# Revit family: 81MAJB-81MBJB-81MCJB-81MDJB_MC Chair_Upholstered Seat Pad Back No Armrest Silver Frame Black Shell_1
name_source: partatom
category: Furniture
revit_build: Autodesk Revit 2017 (Build: 20160225_1515(x64)
units: mm (PartAtom-declared; Revit-internal decimal feet)

## family parameters
Always vertical = Yes
Cut with Voids When Loaded = No
OmniClass Number = 23.40.20.00
OmniClass Title = General Furniture and Specialties
Room Calculation Point = No
Shared = No
Work Plane-Based = No

## types (48) — shared parameters
Assembly Code = E2020200
Caster = okm_G155
D = 580 mm  [stored 1.90289 ft]
Frame = okm_silver FX4
H = 850 mm  [stored 2.78871 ft]
Keynote = 12490
Kind = Chair
Manufacturer = Okamura Corporation
Product Categories = Multi-Purpose Chair
Shell = okm_G721
URL = http://www.okamura.co.jp
W = 596 mm  [stored 1.95538 ft]

## per-type parameters (varying)
| type | Back & Seat | Product Number |
| FEA3（White）_Without Brake Hard Caster | okm_FEA3 | 81MAJB |
| FEA2(Beige)_Without Brake Hard Caster | okm_FEA2 | 81MAJB |
| FGE8(Dark Brown)_Without Brake Hard Caster | okm_FGE8 | 81MAJB |
| FBA3(Light Gray)_Without Brake Hard Caster | okm_FBA3 | 81MAJB |
| FPE2(Medium Gray)_Without Brake Hard Caster | okm_FPE2 | 81MAJB |
| FBA1(Black)_Without Brake Hard Caster | okm_FBA1 | 81MAJB |
| FEA0(Purple)_Without Brake Hard Caster | okm_FEA0 | 81MAJB |
| FBA4(Dark Blue)_Without Brake Hard Caster | okm_FBA4 | 81MAJB |
| FPE6(Sage)_Without Brake Hard Caster | okm_FPE6 | 81MAJB |
| FPE5(Dark Green)_Without Brake Hard Caster | okm_FPE5 | 81MAJB |
| FPE8(Orange Red)_Without Brake Hard Caster | okm_FPE8 | 81MAJB |
| FPE9(Red)_Without Brake Hard Caster | okm_FPE9 | 81MAJB |
| FEA3（White）_With Brake Hard Caster | okm_FEA3 | 81MBJB |
| FEA2(Beige)_With Brake Hard Caster | okm_FEA2 | 81MBJB |
| FGE8(Dark Brown)_With Brake Hard Caster | okm_FGE8 | 81MBJB |
| FBA3(Light Gray)_With Brake Hard Caster | okm_FBA3 | 81MBJB |
| FPE2(Medium Gray)_With Brake Hard Caster | okm_FPE2 | 81MBJB |
| FBA1(Black)_With Brake Hard Caster | okm_FBA1 | 81MBJB |
| FEA0(Purple)_With Brake Hard Caster | okm_FEA0 | 81MBJB |
| FBA4(Dark Blue)_With Brake Hard Caster | okm_FBA4 | 81MBJB |
| FPE6(Sage)_With Brake Hard Caster | okm_FPE6 | 81MBJB |
| FPE5(Dark Green)_With Brake Hard Caster | okm_FPE5 | 81MBJB |
| FPE8(Orange Red)_With Brake Hard Caster | okm_FPE8 | 81MBJB |
| FPE9(Red)_With Brake Hard Caster | okm_FPE9 | 81MBJB |
| FEA3（White）_Without Brake Soft Caster | okm_FEA3 | 81MCJB |
| FEA2(Beige)_Without Brake Soft Caster | okm_FEA2 | 81MCJB |
| FGE8(Dark Brown)_Without Brake Soft Caster | okm_FGE8 | 81MCJB |
| FBA3(Light Gray)_Without Brake Soft Caster | okm_FBA3 | 81MCJB |
| FPE2(Medium Gray)_Without Brake Soft Caster | okm_FPE2 | 81MCJB |
| FBA1(Black)_Without Brake Soft Caster | okm_FBA1 | 81MCJB |
| FEA0(Purple)_Without Brake Soft Caster | okm_FEA0 | 81MCJB |
| FBA4(Dark Blue)_Without Brake Soft Caster | okm_FBA4 | 81MCJB |
| FPE6(Sage)_Without Brake Soft Caster | okm_FPE6 | 81MCJB |
| FPE5(Dark Green)_Without Brake Soft Caster | okm_FPE5 | 81MCJB |
| FPE8(Orange Red)_Without Brake Soft Caster | okm_FPE8 | 81MCJB |
| FPE9(Red)_Without Brake Soft Caster | okm_FPE9 | 81MCJB |
| FEA3（White）_With Brake Soft Caster | okm_FEA3 | 81MDJB |
| FEA2(Beige)_With Brake Soft Caster | okm_FEA2 | 81MDJB |
| FGE8(Dark Brown)_With Brake Soft Caster | okm_FGE8 | 81MDJB |
| FBA3(Light Gray)_With Brake Soft Caster | okm_FBA3 | 81MDJB |
| FPE2(Medium Gray)_With Brake Soft Caster | okm_FPE2 | 81MDJB |
| FBA1(Black)_With Brake Soft Caster | okm_FBA1 | 81MDJB |
| FEA0(Purple)_With Brake Soft Caster | okm_FEA0 | 81MDJB |
| FBA4(Dark Blue)_With Brake Soft Caster | okm_FBA4 | 81MDJB |
| FPE6(Sage)_With Brake Soft Caster | okm_FPE6 | 81MDJB |
| FPE5(Dark Green)_With Brake Soft Caster | okm_FPE5 | 81MDJB |
| FPE8(Orange Red)_With Brake Soft Caster | okm_FPE8 | 81MDJB |
| FPE9(Red)_With Brake Soft Caster | okm_FPE9 | 81MDJB |

note: [stored X ft] marks values corroborated as IEEE doubles in the binary element streams (Revit-internal decimal feet)
